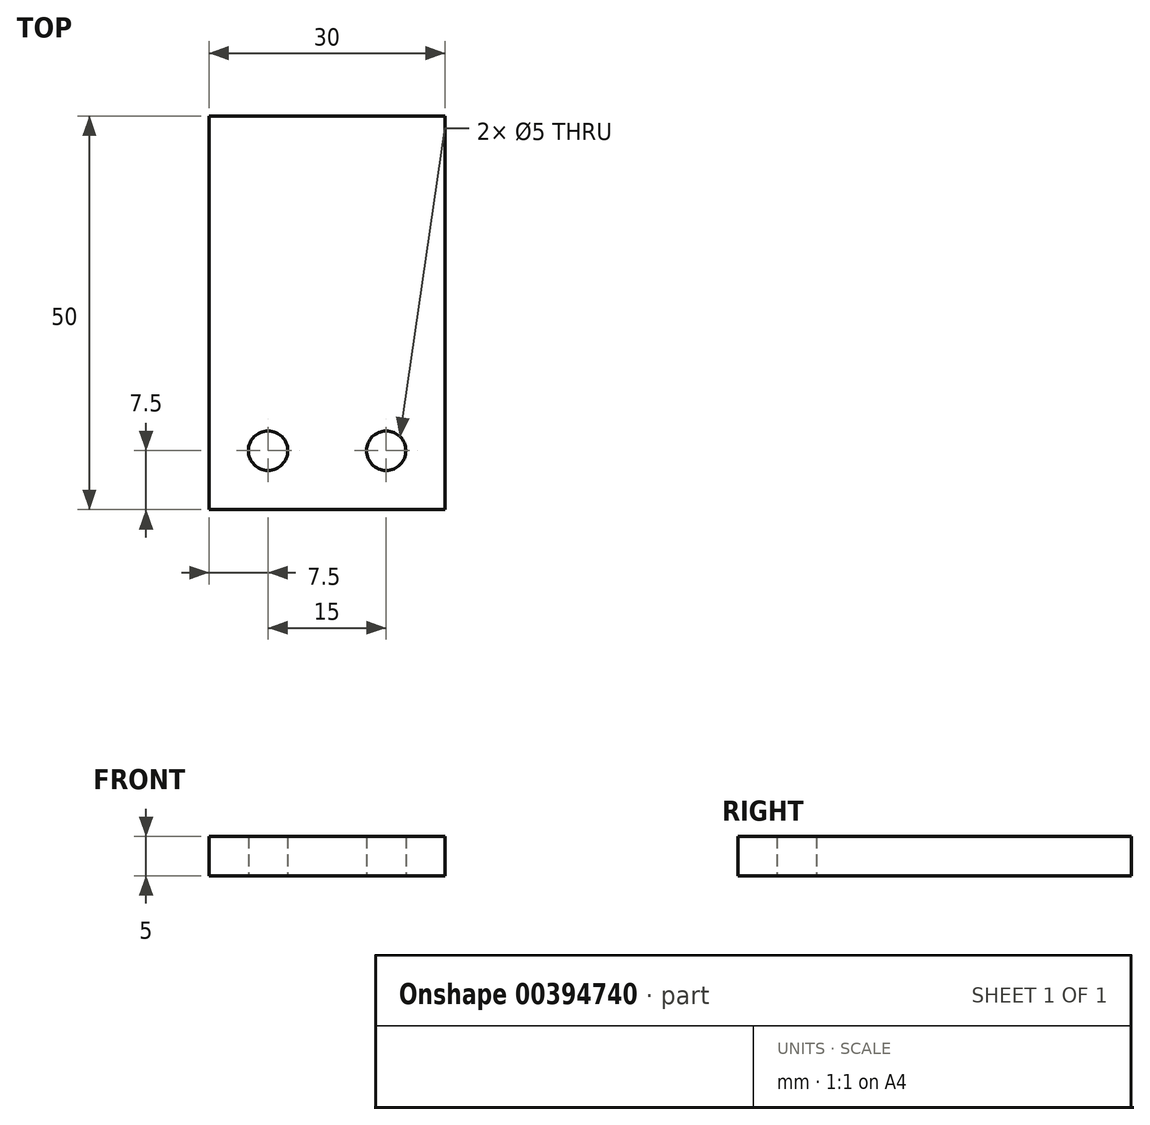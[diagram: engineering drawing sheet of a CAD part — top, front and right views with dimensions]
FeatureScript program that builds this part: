
annotation { "Feature Type Name" : "Feature", "Feature Type Description" : "" }
export const myFeature = defineFeature(function(context is Context, id is Id, definition is map)
    precondition{}
    {
        {
            var Q0;
            Q0=qCreatedBy(makeId("Top.planeOp"),FACE);
            var sketch = newSketch(context, id + "F0", { "sketchPlane" : qUnion([Q0])});
            skLineSegment(sketch, "E0.bottom", {"start": v(-15, 25) * mm, "end": v(15, 25) * mm});
            skLineSegment(sketch, "E0.top", {"start": v(-15, -25) * mm, "end": v(15, -25) * mm});
            skLineSegment(sketch, "E0.left", {"start": v(-15, 25) * mm, "end": v(-15, -25) * mm});
            skLineSegment(sketch, "E0.right", {"start": v(15, 25) * mm, "end": v(15, -25) * mm});
            skPoint(sketch, "E0.middle", {"position": v(0, 0) * mm});
            skLineSegment(sketch, "E1", {"start": v(0, 0) * mm, "end": v(0, 25) * mm, "construction": true});
            skCircle(sketch, "E2", {"center": v(-7.5, -17.5) * mm, "radius": 2.5 * mm});
            skCircle(sketch, "E3.MirrorC", {"center": v(7.5, -17.5) * mm, "radius": 2.5 * mm});
            skSolve(sketch);
        }
        {
            var Q0;
            Q0=makeQuery(id+"F0.imprint","IMPRINT",FACE,{"disambiguationData":[TD([[makeQuery(id+"F0.imprint","IMPRINT",EDGE,{"derivedFrom":sQuery(id+"F0.wireOp",EDGE,"E0.bottom")}),-1.0]])]});
            extrude(context, id + "F1", {"entities" : qUnion([Q0]), "depth" : 5 * mm});
        }
    });
